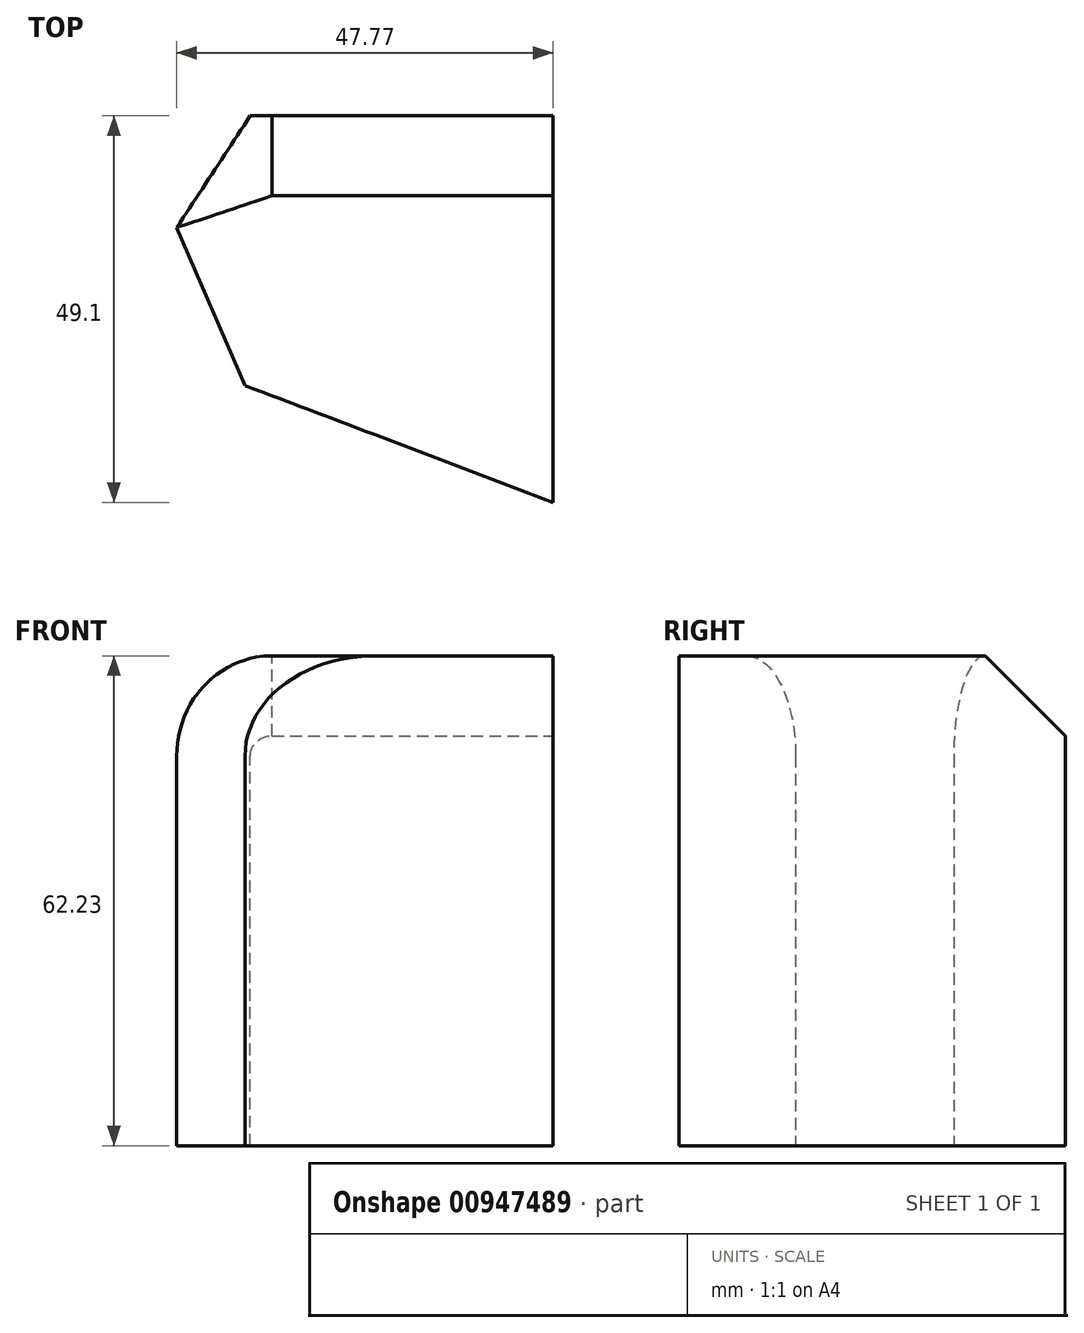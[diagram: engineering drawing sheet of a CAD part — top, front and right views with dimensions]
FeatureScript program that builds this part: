
annotation { "Feature Type Name" : "Feature", "Feature Type Description" : "" }
export const myFeature = defineFeature(function(context is Context, id is Id, definition is map)
    precondition{}
    {
        {
            var Q0;
            Q0=qCreatedBy(makeId("Top.planeOp"),FACE);
            var sketch = newSketch(context, id + "F0", { "sketchPlane" : qUnion([Q0])});
            skLineSegment(sketch, "E0", {"start": v(0, 0) * mm, "end": v(53.87, 0) * mm});
            skLineSegment(sketch, "E1", {"start": v(53.87, 0) * mm, "end": v(53.87, -49.1) * mm});
            skLineSegment(sketch, "E2", {"start": v(53.87, -49.1) * mm, "end": v(14.74, -34.26) * mm});
            skLineSegment(sketch, "E3", {"start": v(14.74, -34.26) * mm, "end": v(0, 0) * mm});
            skSolve(sketch);
        }
        {
            var Q0;
            Q0 = qSketchRegion(id + "F0", true);
            var Q1;
            Q1=makeQuery(id+"F0.imprint","IMPRINT",FACE,{"disambiguationData":[TD([[makeQuery(id+"F0.imprint","IMPRINT",EDGE,{"derivedFrom":sQuery(id+"F0.wireOp",EDGE,"E0")}),-1.0]])]});
            extrude(context, id + "F1", {"entities" : qUnion([Q0, Q1]), "depth" : 62.23 * mm, "offsetDistance" : 25.4 * mm});
        }
        {
            var Q0;
            Q0=makeQuery(id+"F1.opExtrude","CAP_EDGE",EDGE,{"disambiguationData":[OSD([sQuery(id+"F0.wireOp",EDGE,"E3")])],"isStart":false});
            fillet(context, id + "F2", {"entities" : qUnion([Q0]), "radius" : 12.7 * mm, "tangentPropagation" : true, "allowEdgeOverflow" : false});
        }
        {
            var Q0;
            Q0=makeQuery(id+"F1.opExtrude","CAP_EDGE",EDGE,{"disambiguationData":[OSD([sQuery(id+"F0.wireOp",EDGE,"E0")])],"isStart":false});
            chamfer(context, id + "F3", {"entities" : qUnion([Q0]), "chamferType" : ChamferType.OFFSET_ANGLE, "width" : 10.16 * mm, "oppositeDirection" : false, "angle" : 45 * degree, "tangentPropagation" : true});
        }
    });
